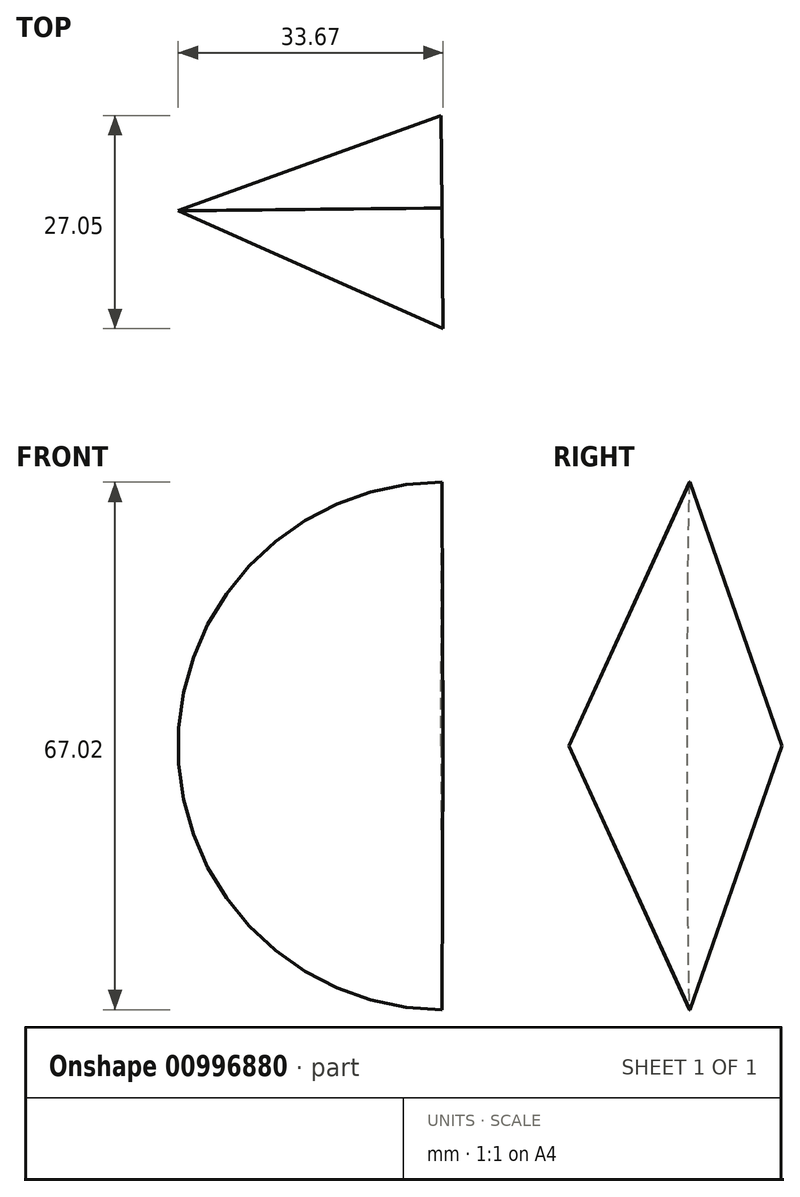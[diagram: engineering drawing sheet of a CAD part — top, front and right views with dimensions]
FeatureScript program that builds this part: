
annotation { "Feature Type Name" : "Feature", "Feature Type Description" : "" }
export const myFeature = defineFeature(function(context is Context, id is Id, definition is map)
    precondition{}
    {
        {
            var Q0;
            Q0=qCreatedBy(makeId("Top.planeOp"),FACE);
            var sketch = newSketch(context, id + "F0", { "sketchPlane" : qUnion([Q0])});
            skLineSegment(sketch, "E0", {"start": v(-45.33, 41.3) * mm, "end": v(-78.71, 29.21) * mm});
            skLineSegment(sketch, "E1", {"start": v(-78.71, 29.21) * mm, "end": v(-45.04, 14.25) * mm});
            skLineSegment(sketch, "E2", {"start": v(-45.04, 14.25) * mm, "end": v(-45.33, 41.3) * mm});
            skSolve(sketch);
        }
        {
            var Q0;
            Q0=makeQuery(id+"F0.imprint","IMPRINT",FACE,{"disambiguationData":[TD([[makeQuery(id+"F0.imprint","IMPRINT",EDGE,{"derivedFrom":sQuery(id+"F0.wireOp",EDGE,"E0")}),1.0]])]});
            var Q1;
            Q1=sQuery(id+"F0.wireOp",EDGE,"E2");
            revolve(context, id + "F1", {"surfaceOperationType" : NewSurfaceOperationType.NEW, "entities" : qUnion([Q0]), "axis" : qUnion([Q1]), "revolveType" : RevolveType.SYMMETRIC, "angle" : 180 * degree});
        }
    });
